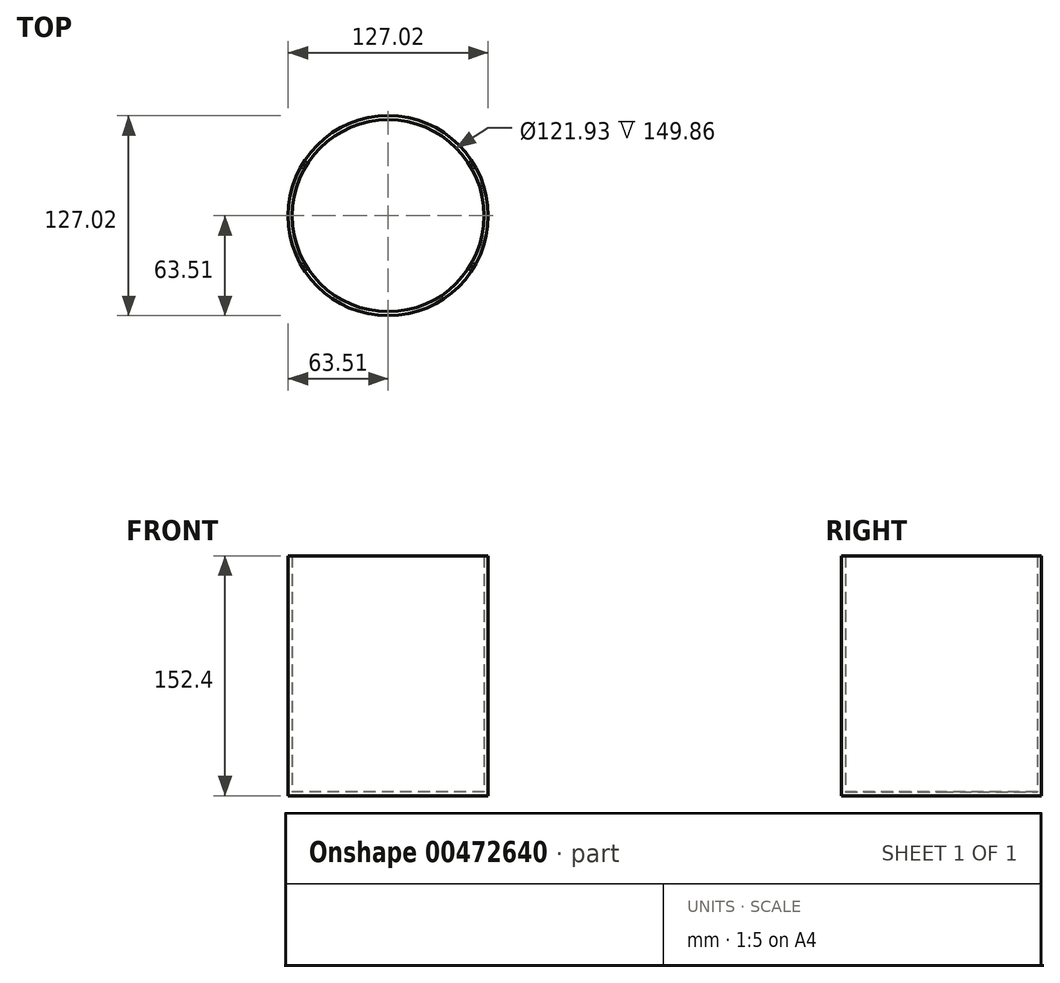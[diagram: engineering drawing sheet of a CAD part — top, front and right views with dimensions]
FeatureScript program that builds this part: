
annotation { "Feature Type Name" : "Feature", "Feature Type Description" : "" }
export const myFeature = defineFeature(function(context is Context, id is Id, definition is map)
    precondition{}
    {
        {
            var Q0;
            Q0=qCreatedBy(makeId("Top.planeOp"),FACE);
            var sketch = newSketch(context, id + "F0", { "sketchPlane" : qUnion([Q0])});
            skCircle(sketch, "E0", {"center": v(0, 0) * mm, "radius": 63.5 * mm});
            skSolve(sketch);
        }
        {
            var Q0;
            Q0 = qSketchRegion(id + "F0", true);
            extrude(context, id + "F1", {"entities" : qUnion([Q0]), "depth" : 76.2 * mm});
        }
        {
            var Q0;
            Q0=makeQuery(id+"F1.opExtrude","CAP_FACE",FACE,{"disambiguationData":[OSD([sQuery(id+"F0.wireOp",EDGE,"E0")])],"isStart":false});
            shell(context, id + "F2", {"entities" : qUnion([Q0]), "thickness" : 2.54 * mm});
        }
        {
            var Q0;
            Q0=makeQuery(id+"F1.opExtrude","CAP_FACE",FACE,{"disambiguationData":[OSD([sQuery(id+"F0.wireOp",EDGE,"E0")])],"isStart":false});
            extrude(context, id + "F3", {"entities" : qUnion([Q0]), "operationType" : NewBodyOperationType.ADD, "depth" : 76.2 * mm});
        }
    });
